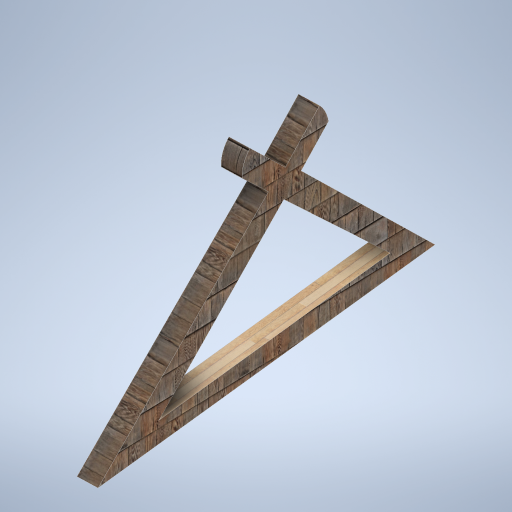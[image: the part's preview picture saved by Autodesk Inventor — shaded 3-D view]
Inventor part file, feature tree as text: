
AUTODESK INVENTOR PART (.ipt)
format: ipt  version: 2024.2 (Build 282272000, 272)  size: 526,336 bytes
history: native  units: mm
features: sketch x12, plane x8, extrude x5, projected_geometry x3, loft x2, other x1
ambient origin geometry x8: Origin, YZ Plane, XZ Plane, XY Plane, X Axis, Y Axis, Z Axis, Center Point
bodies: Solid1 (feature_tree)
feature tree (31):
  sketch  "Sketch1"  dims[d5=0.0mm d6=-7900.0mm d7=800.0mm]
  plane  "Work Plane2"
  loft  "Loft1"
  plane  "Work Plane3"
  extrude  "Extrusion1"  Depth=9000.0mm
  plane  "Work Plane4"
  sketch  "Sketch5"  dims[d12=800.0mm d13=0.0mm d14=90.0deg]
  plane  "Work Plane5"
  extrude  "Extrusion2"  Depth=9000.0mm
  plane  "Work Plane6"
  sketch  "Sketch7"  dims[d18=0.0mm d19=0.0mm d20=0.0mm]
  loft  "Loft2"
  extrude  "Extrusion3"  Depth=2500.0mm
  sketch  "Sketch10"  dims[d25=0.0mm d26=90.0deg]
  extrude  "Extrusion4"  TaperAngle=0.0deg  [1 undecoded]
  plane  "Work Plane7"
  extrude  "Extrusion5"  TaperAngle=0.0deg  [1 undecoded]
  plane  "Work Plane8"
  sketch  "Sketch14"  dims[d31=0.0mm d32=0.0mm d35=150.0mm d36=0.0mm d37=-75.0mm d38=500.0mm d39=0.872665mm d40=500.0mm d41=0.872665mm]
  plane  "Work Plane1"
  sketch  "Sketch2"  dims[d8=9000.0mm d9=9000.0mm]
  sketch  "Sketch3"  dims[d10=9000.0mm d11=9000.0mm]
  sketch  "Sketch6"  dims[d15=0.0mm d16=90.0deg d17=2500.0mm]
  projected_geometry  "Projected Loop1"
  sketch  "Sketch8"  dims[d21=6.981317mm d22=0.0mm d23=0.0mm]
  projected_geometry  "Projected Loop2"
  other  "Edges1"
  sketch  "Sketch9"  dims[d24=90.0deg]
  projected_geometry  "Projected Loop3"
  sketch  "Sketch11"  dims[d27=0.0mm d28=90.0deg]
  sketch  "Sketch12"  dims[d29=1.0mm d30=0.0mm]
note: 2 required parameter values undecoded (feature->parameter linkage not recoverable at this tier; creation-order binding heuristic only, values carry confidence <= 0.55)
